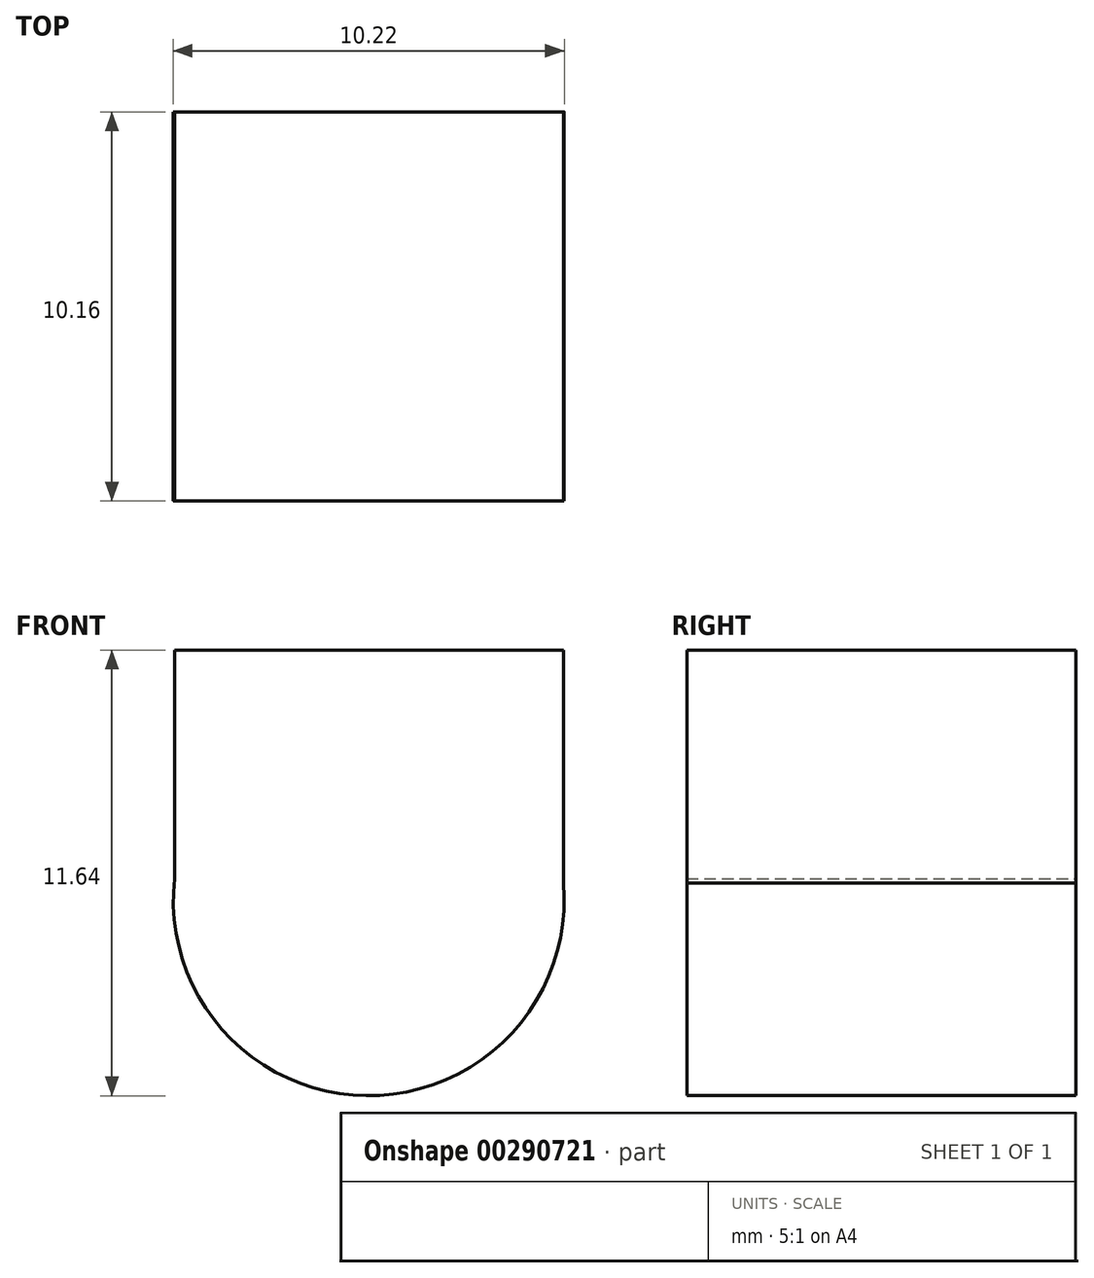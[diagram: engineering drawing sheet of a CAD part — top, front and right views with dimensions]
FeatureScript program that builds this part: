
annotation { "Feature Type Name" : "Feature", "Feature Type Description" : "" }
export const myFeature = defineFeature(function(context is Context, id is Id, definition is map)
    precondition{}
    {
        {
            var Q0;
            Q0=qCreatedBy(makeId("Front.planeOp"),FACE);
            var sketch = newSketch(context, id + "F0", { "sketchPlane" : qUnion([Q0])});
            skLineSegment(sketch, "E0", {"start": v(-5.07, 6.53) * mm, "end": v(5.09, 6.53) * mm});
            skLineSegment(sketch, "E1", {"start": v(5.09, 6.53) * mm, "end": v(5.09, 0) * mm});
            skLineSegment(sketch, "E2", {"start": v(-5.07, 6.53) * mm, "end": v(-5.07, 0) * mm});
            skCircle(sketch, "E3", {"center": v(0, 0) * mm, "radius": 5.1 * mm});
            skPoint(sketch, "E4", {"position": v(0, 6.53) * mm});
            skPoint(sketch, "E5", {"position": v(0, -5.1) * mm});
            skSolve(sketch);
        }
        {
            var Q0;
            {var subQ0=sQuery(id+"F0.wireOp",EDGE,"E0");Q0=makeQuery(id+"F0.imprint","IMPRINT",FACE,{"disambiguationData":[TD([[makeQuery(id+"F0.imprint","IMPRINT",EDGE,{"derivedFrom":subQ0}),-1.0]])]});}
            extrude(context, id + "F1", {"entities" : qUnion([Q0]), "depth" : 10.16 * mm});
        }
        {
            var Q0;
            {var subQ0=sQuery(id+"F0.wireOp",EDGE,"E3");var subQ1=makeQuery(id+"F0.imprint","INTERSECT",VERTEX,{"derivedFrom":[sQuery(id+"F0.wireOp",EDGE,"E1"),subQ0]});Q0=makeQuery(id+"F0.imprint","IMPRINT",FACE,{"disambiguationData":[TD([[makeQuery(id+"F0.imprint","IMPRINT",EDGE,{"disambiguationData":[TD([[subQ1,-1.0]])],"derivedFrom":subQ0}),1.0]])]});}
            extrude(context, id + "F2", {"entities" : qUnion([Q0]), "operationType" : NewBodyOperationType.ADD, "depth" : 10.16 * mm});
        }
    });
